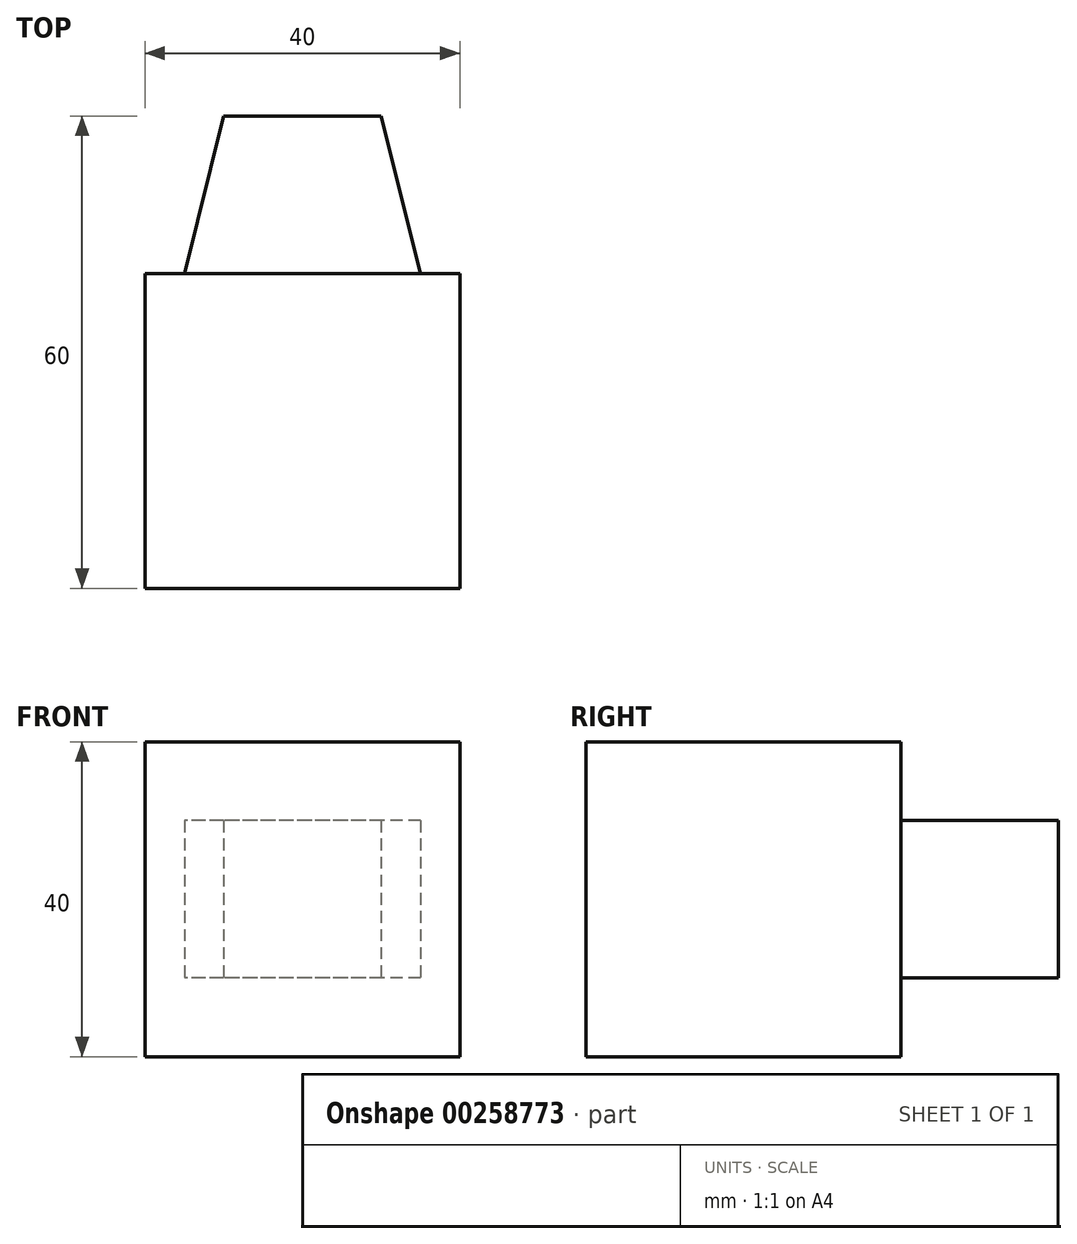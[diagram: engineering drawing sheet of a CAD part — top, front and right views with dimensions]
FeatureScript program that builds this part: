
annotation { "Feature Type Name" : "Feature", "Feature Type Description" : "" }
export const myFeature = defineFeature(function(context is Context, id is Id, definition is map)
    precondition{}
    {
        {
            var Q0;
            Q0=qCreatedBy(makeId("Front.planeOp"),FACE);
            var sketch = newSketch(context, id + "F0", { "sketchPlane" : qUnion([Q0])});
            skLineSegment(sketch, "E0.bottom", {"start": v(20, -20) * mm, "end": v(-20, -20) * mm});
            skLineSegment(sketch, "E0.top", {"start": v(20, 20) * mm, "end": v(-20, 20) * mm});
            skLineSegment(sketch, "E0.left", {"start": v(20, -20) * mm, "end": v(20, 20) * mm});
            skLineSegment(sketch, "E0.right", {"start": v(-20, -20) * mm, "end": v(-20, 20) * mm});
            skPoint(sketch, "E0.middle", {"position": v(0, 0) * mm});
            skSolve(sketch);
        }
        {
            var Q0;
            Q0=makeQuery(id+"F0.imprint","IMPRINT",FACE,{"disambiguationData":[TD([[makeQuery(id+"F0.imprint","IMPRINT",EDGE,{"derivedFrom":sQuery(id+"F0.wireOp",EDGE,"E0.bottom")}),-1.0]])]});
            extrude(context, id + "F1", {"entities" : qUnion([Q0]), "depth" : 40 * mm});
        }
        {
            var Q0;
            Q0=qCreatedBy(makeId("Top.planeOp"),FACE);
            var sketch = newSketch(context, id + "F2", { "sketchPlane" : qUnion([Q0])});
            skLineSegment(sketch, "E1", {"start": v(15, 0) * mm, "end": v(-15, 0) * mm});
            skLineSegment(sketch, "E2", {"start": v(10, 20) * mm, "end": v(-10, 20) * mm});
            skLineSegment(sketch, "E3", {"start": v(-10, 20) * mm, "end": v(-15, 0) * mm});
            skLineSegment(sketch, "E4", {"start": v(15, 0) * mm, "end": v(10, 20) * mm});
            skLineSegment(sketch, "E5", {"start": v(0, 0) * mm, "end": v(0, 20) * mm});
            skSolve(sketch);
        }
        {
            var Q0;
            Q0=makeQuery(id+"F2.imprint","IMPRINT",FACE,{"disambiguationData":[TD([[makeQuery(id+"F2.imprint","IMPRINT",EDGE,{"derivedFrom":sQuery(id+"F2.wireOp",EDGE,"E1")}),-1.0]])]});
            extrude(context, id + "F3", {"entities" : qUnion([Q0]), "operationType" : NewBodyOperationType.ADD, "endBound" : BoundingType.SYMMETRIC, "depth" : 20 * mm});
        }
    });
